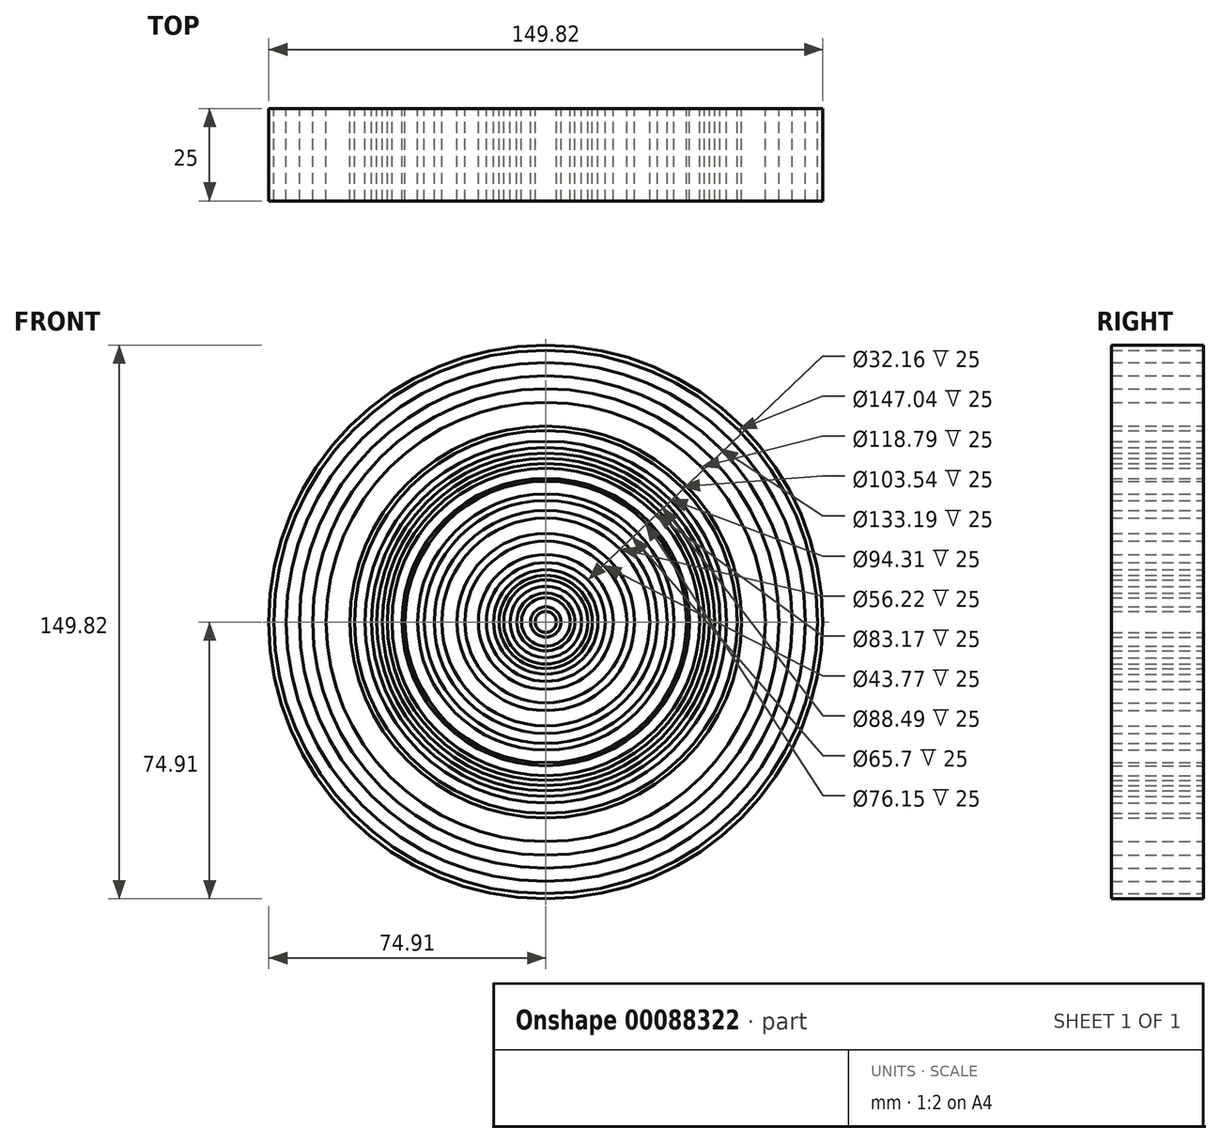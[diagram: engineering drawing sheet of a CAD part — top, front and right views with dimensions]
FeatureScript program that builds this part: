
annotation { "Feature Type Name" : "Feature", "Feature Type Description" : "" }
export const myFeature = defineFeature(function(context is Context, id is Id, definition is map)
    precondition{}
    {
        {
            var Q0;
            Q0=qCreatedBy(makeId("Front.planeOp"),FACE);
            var sketch = newSketch(context, id + "F0", { "sketchPlane" : qUnion([Q0])});
            skCircle(sketch, "E0", {"center": v(0, 0) * mm, "radius": 74.91 * mm});
            skCircle(sketch, "E1", {"center": v(0, 0) * mm, "radius": 59.4 * mm});
            skCircle(sketch, "E2", {"center": v(0, 0) * mm, "radius": 39.9 * mm});
            skCircle(sketch, "E3", {"center": v(0, 0) * mm, "radius": 25.74 * mm});
            skCircle(sketch, "E4", {"center": v(0, 0) * mm, "radius": 20.1 * mm});
            skCircle(sketch, "E5", {"center": v(0, 0) * mm, "radius": 73.52 * mm});
            skCircle(sketch, "E6", {"center": v(0, 0) * mm, "radius": 71.86 * mm});
            skCircle(sketch, "E7", {"center": v(0, 0) * mm, "radius": 70.2 * mm});
            skCircle(sketch, "E8", {"center": v(0, 0) * mm, "radius": 2.85 * mm});
            skCircle(sketch, "E9", {"center": v(0, 0) * mm, "radius": 5.34 * mm});
            skCircle(sketch, "E10", {"center": v(0, 0) * mm, "radius": 7.85 * mm});
            skCircle(sketch, "E11", {"center": v(0, 0) * mm, "radius": 9.66 * mm});
            skCircle(sketch, "E12", {"center": v(0, 0) * mm, "radius": 18.24 * mm});
            skCircle(sketch, "E13", {"center": v(0, 0) * mm, "radius": 16.08 * mm});
            skCircle(sketch, "E14", {"center": v(0, 0) * mm, "radius": 12.61 * mm});
            skCircle(sketch, "E15", {"center": v(0, 0) * mm, "radius": 14.11 * mm});
            skCircle(sketch, "E16", {"center": v(0, 0) * mm, "radius": 52.98 * mm});
            skCircle(sketch, "E17", {"center": v(0, 0) * mm, "radius": 1.6 * mm});
            skCircle(sketch, "E18", {"center": v(0, 0) * mm, "radius": 28.1 * mm});
            skCircle(sketch, "E19", {"center": v(0, 0) * mm, "radius": 21.88 * mm});
            skCircle(sketch, "E20", {"center": v(0, 0) * mm, "radius": 23.98 * mm});
            skCircle(sketch, "E21", {"center": v(0, 0) * mm, "radius": 4.12 * mm});
            skCircle(sketch, "E22", {"center": v(0, 0) * mm, "radius": 11.37 * mm});
            skCircle(sketch, "E23", {"center": v(0, 0) * mm, "radius": 6.57 * mm});
            skCircle(sketch, "E24", {"center": v(0, 0) * mm, "radius": 30.16 * mm});
            skCircle(sketch, "E25", {"center": v(0, 0) * mm, "radius": 31.43 * mm});
            skCircle(sketch, "E26", {"center": v(0, 0) * mm, "radius": 32.85 * mm});
            skCircle(sketch, "E27", {"center": v(0, 0) * mm, "radius": 34.66 * mm});
            skCircle(sketch, "E28", {"center": v(0, 0) * mm, "radius": 37.04 * mm});
            skCircle(sketch, "E29", {"center": v(0, 0) * mm, "radius": 38.86 * mm});
            skCircle(sketch, "E30", {"center": v(0, 0) * mm, "radius": 35.86 * mm});
            skCircle(sketch, "E31", {"center": v(0, 0) * mm, "radius": 38.08 * mm});
            skCircle(sketch, "E32", {"center": v(0, 0) * mm, "radius": 68.42 * mm});
            skCircle(sketch, "E33", {"center": v(0, 0) * mm, "radius": 66.6 * mm});
            skCircle(sketch, "E34", {"center": v(0, 0) * mm, "radius": 41.59 * mm});
            skCircle(sketch, "E35", {"center": v(0, 0) * mm, "radius": 42.87 * mm});
            skCircle(sketch, "E36", {"center": v(0, 0) * mm, "radius": 44.24 * mm});
            skCircle(sketch, "E37", {"center": v(0, 0) * mm, "radius": 51.77 * mm});
            skCircle(sketch, "E38", {"center": v(0, 0) * mm, "radius": 50.07 * mm});
            skCircle(sketch, "E39", {"center": v(0, 0) * mm, "radius": 48.9 * mm});
            skCircle(sketch, "E40", {"center": v(0, 0) * mm, "radius": 45.7 * mm});
            skCircle(sketch, "E41", {"center": v(0, 0) * mm, "radius": 47.16 * mm});
            skCircle(sketch, "E42", {"center": v(0, 0) * mm, "radius": 56.5 * mm});
            skCircle(sketch, "E43", {"center": v(0, 0) * mm, "radius": 63.07 * mm});
            skSolve(sketch);
        }
        {
            var Q0;
            Q0 = qSketchRegion(id + "F0", true);
            var Q1;
            Q1=makeQuery(id+"F0.imprint","IMPRINT",FACE,{"disambiguationData":[TD([[makeQuery(id+"F0.imprint","IMPRINT",EDGE,{"derivedFrom":sQuery(id+"F0.wireOp",EDGE,"E10")}),1.0]])]});
            var Q2;
            Q2=makeQuery(id+"F0.imprint","IMPRINT",FACE,{"disambiguationData":[TD([[makeQuery(id+"F0.imprint","IMPRINT",EDGE,{"derivedFrom":sQuery(id+"F0.wireOp",EDGE,"E19")}),-1.0]])]});
            var Q3;
            Q3=makeQuery(id+"F0.imprint","IMPRINT",FACE,{"disambiguationData":[TD([[makeQuery(id+"F0.imprint","IMPRINT",EDGE,{"derivedFrom":sQuery(id+"F0.wireOp",EDGE,"E26")}),-1.0]])]});
            var Q4;
            Q4=makeQuery(id+"F0.imprint","IMPRINT",FACE,{"disambiguationData":[TD([[makeQuery(id+"F0.imprint","IMPRINT",EDGE,{"derivedFrom":sQuery(id+"F0.wireOp",EDGE,"E18")}),-1.0]])]});
            var Q5;
            Q5=makeQuery(id+"F0.imprint","IMPRINT",FACE,{"disambiguationData":[TD([[makeQuery(id+"F0.imprint","IMPRINT",EDGE,{"derivedFrom":sQuery(id+"F0.wireOp",EDGE,"E14")}),-1.0]])]});
            var Q6;
            Q6=makeQuery(id+"F0.imprint","IMPRINT",FACE,{"disambiguationData":[TD([[makeQuery(id+"F0.imprint","IMPRINT",EDGE,{"derivedFrom":sQuery(id+"F0.wireOp",EDGE,"E11")}),-1.0]])]});
            var Q7;
            Q7=makeQuery(id+"F0.imprint","IMPRINT",FACE,{"disambiguationData":[TD([[makeQuery(id+"F0.imprint","IMPRINT",EDGE,{"derivedFrom":sQuery(id+"F0.wireOp",EDGE,"E29")}),1.0]])]});
            var Q8;
            Q8=makeQuery(id+"F0.imprint","IMPRINT",FACE,{"disambiguationData":[TD([[makeQuery(id+"F0.imprint","IMPRINT",EDGE,{"derivedFrom":sQuery(id+"F0.wireOp",EDGE,"E34")}),-1.0]])]});
            var Q9;
            Q9=makeQuery(id+"F0.imprint","IMPRINT",FACE,{"disambiguationData":[TD([[makeQuery(id+"F0.imprint","IMPRINT",EDGE,{"derivedFrom":sQuery(id+"F0.wireOp",EDGE,"E39")}),1.0]])]});
            var Q10;
            Q10=makeQuery(id+"F0.imprint","IMPRINT",FACE,{"disambiguationData":[TD([[makeQuery(id+"F0.imprint","IMPRINT",EDGE,{"derivedFrom":sQuery(id+"F0.wireOp",EDGE,"E16")}),1.0]])]});
            var Q11;
            Q11=makeQuery(id+"F0.imprint","IMPRINT",FACE,{"disambiguationData":[TD([[makeQuery(id+"F0.imprint","IMPRINT",EDGE,{"derivedFrom":sQuery(id+"F0.wireOp",EDGE,"E1")}),-1.0]])]});
            var Q12;
            Q12=makeQuery(id+"F0.imprint","IMPRINT",FACE,{"disambiguationData":[TD([[makeQuery(id+"F0.imprint","IMPRINT",EDGE,{"derivedFrom":sQuery(id+"F0.wireOp",EDGE,"E7")}),1.0]])]});
            var Q13;
            Q13=makeQuery(id+"F0.imprint","IMPRINT",FACE,{"disambiguationData":[TD([[makeQuery(id+"F0.imprint","IMPRINT",EDGE,{"derivedFrom":sQuery(id+"F0.wireOp",EDGE,"E32")}),1.0]])]});
            var Q14;
            Q14=makeQuery(id+"F0.imprint","IMPRINT",FACE,{"disambiguationData":[TD([[makeQuery(id+"F0.imprint","IMPRINT",EDGE,{"derivedFrom":sQuery(id+"F0.wireOp",EDGE,"E36")}),-1.0]])]});
            var Q15;
            Q15=makeQuery(id+"F0.imprint","IMPRINT",FACE,{"disambiguationData":[TD([[makeQuery(id+"F0.imprint","IMPRINT",EDGE,{"derivedFrom":sQuery(id+"F0.wireOp",EDGE,"E12")}),1.0]])]});
            var Q16;
            Q16=makeQuery(id+"F0.imprint","IMPRINT",FACE,{"disambiguationData":[TD([[makeQuery(id+"F0.imprint","IMPRINT",EDGE,{"derivedFrom":sQuery(id+"F0.wireOp",EDGE,"E8")}),-1.0]])]});
            extrude(context, id + "F1", {"entities" : qUnion([Q0, Q1, Q2, Q3, Q4, Q5, Q6, Q7, Q8, Q9, Q10, Q11, Q12, Q13, Q14, Q15, Q16]), "depth" : 25 * mm});
        }
    });
